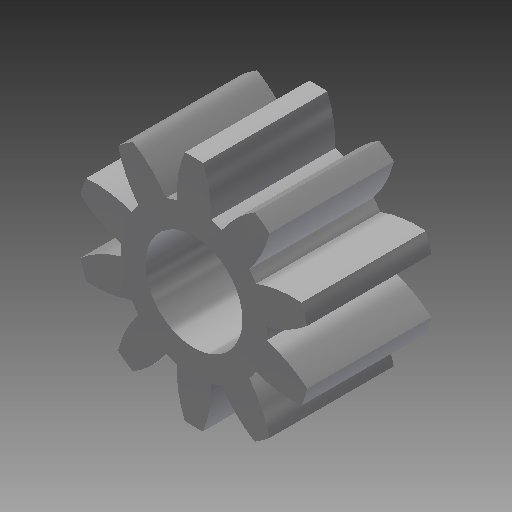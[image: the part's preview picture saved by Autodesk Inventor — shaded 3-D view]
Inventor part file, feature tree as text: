
AUTODESK INVENTOR PART (.ipt)
format: ipt  version: 2019 (Build 230136000, 136)  size: 203,264 bytes
history: native  units: mm (DEFAULTED — no unit token found)
features: plane x3, other x3, sketch x3, extrude x1, hole x1
ambient origin geometry x8: Origin, YZ Plane, XZ Plane, XY Plane, X Axis, Y Axis, Z Axis, Center Point
bodies: Solid1 (feature_tree)
feature tree (11):
  extrude  "Extrusion1"  Depth=3.2mm TaperAngle=0.0deg
  plane  "Work Plane2"
  plane  "Work Plane8"
  plane  "Work Plane9"
  other  "Przekładnia walcowa"
  hole  "Otwór1"  [1 undecoded]
  sketch  "Sketch1"  dims[d0=6.0mm d1=3.2mm d2=0.0mm]
  sketch  "Sketch2"  dims[d3=5.0mm d4=10.0mm d5=0.0mm d16=10.0mm d17=0.0mm d34=3.141593mm d39=0.0mm d41=0.0mm d43=10.0mm d46=10.0mm d47=0.0mm d48=0.0mm d49=2.5mm d50=6.0mm d51=4.0mm d52=2.0mm d53=90.0deg d54=8.0mm d55=20.594885mm]
  other  "Srf1"
  sketch  "Szkic3"
  other  "Średnica podziałowa"
note: 1 required parameter value undecoded (feature->parameter linkage not recoverable at this tier; creation-order binding heuristic only, values carry confidence <= 0.55)
